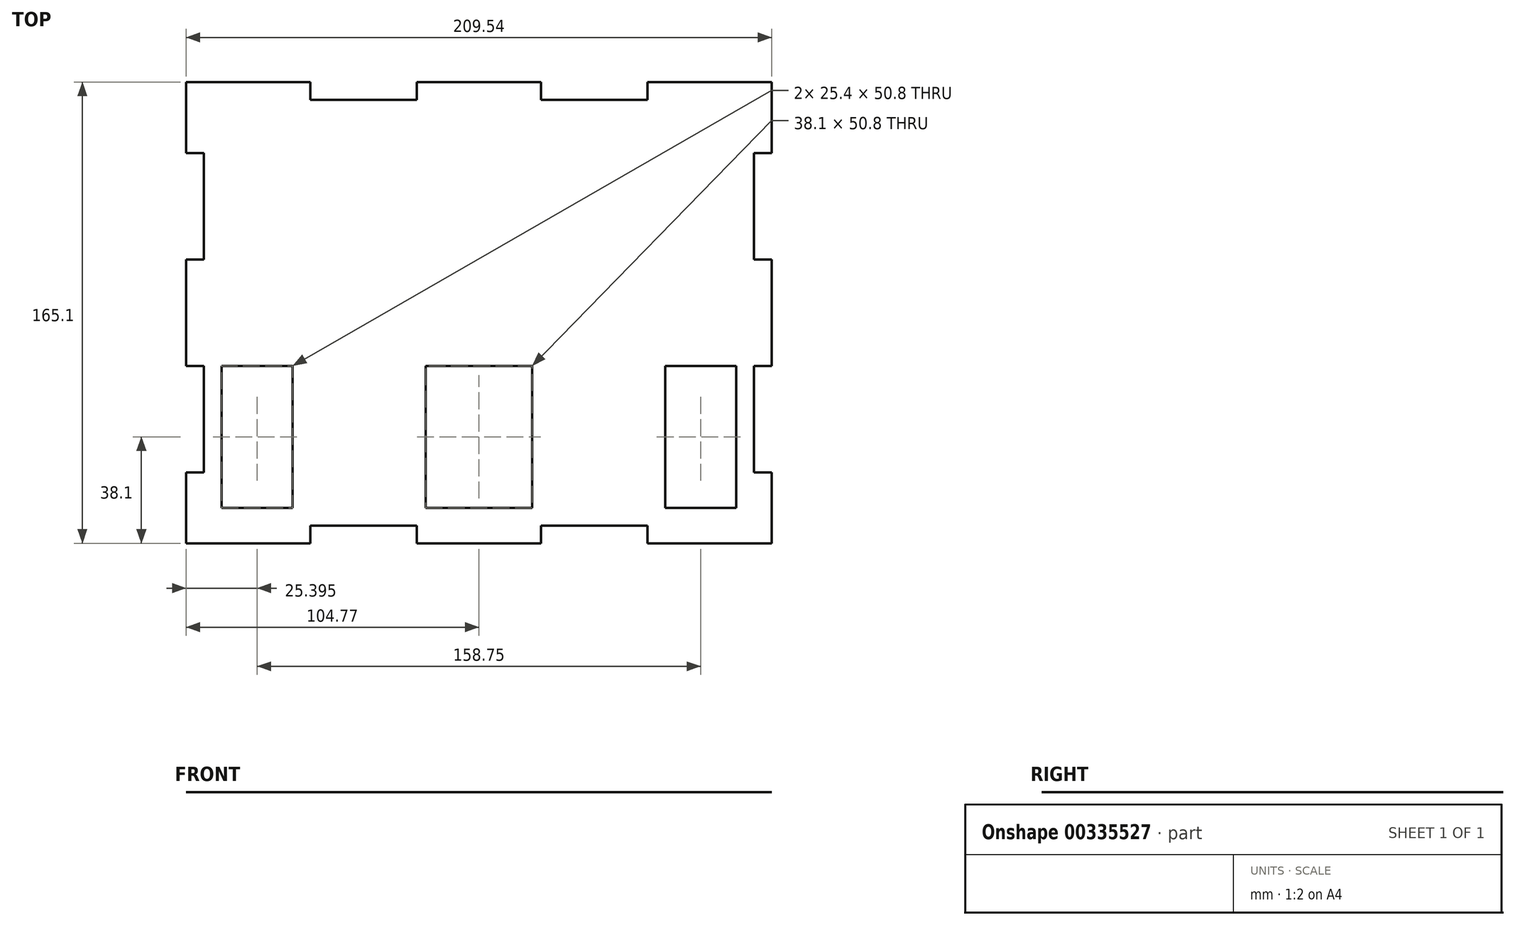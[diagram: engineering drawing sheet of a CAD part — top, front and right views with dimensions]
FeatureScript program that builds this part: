
annotation { "Feature Type Name" : "Feature", "Feature Type Description" : "" }
export const myFeature = defineFeature(function(context is Context, id is Id, definition is map)
    precondition{}
    {
        {
            var Q0;
            Q0=qCreatedBy(makeId("Top.planeOp"),FACE);
            var sketch = newSketch(context, id + "F0", { "sketchPlane" : qUnion([Q0])});
            skLineSegment(sketch, "E0.bottom", {"start": v(104.78, -82.55) * mm, "end": v(-104.77, -82.55) * mm});
            skLineSegment(sketch, "E0.top", {"start": v(104.77, 82.55) * mm, "end": v(-104.78, 82.55) * mm});
            skLineSegment(sketch, "E0.left", {"start": v(104.78, -82.55) * mm, "end": v(104.77, 82.55) * mm});
            skLineSegment(sketch, "E0.right", {"start": v(-104.77, -82.55) * mm, "end": v(-104.78, 82.55) * mm});
            skPoint(sketch, "E0.middle", {"position": v(0, 0) * mm});
            skSolve(sketch);
        }
        {
            var Q0;
            Q0=makeQuery(id+"F0.imprint","IMPRINT",FACE,{"disambiguationData":[TD([[makeQuery(id+"F0.imprint","IMPRINT",EDGE,{"derivedFrom":sQuery(id+"F0.wireOp",EDGE,"E0.bottom")}),-1.0]])]});
            extrude(context, id + "F1", {"entities" : qUnion([Q0]), "depth" : 1 / 203.2 * mm});
        }
        {
            var Q0;
            Q0=makeQuery(id+"F1.opExtrude","CAP_FACE",FACE,{"disambiguationData":[OSD([sQuery(id+"F0.wireOp",EDGE,"E0.bottom"),sQuery(id+"F0.wireOp",EDGE,"E0.top"),sQuery(id+"F0.wireOp",EDGE,"E0.left"),sQuery(id+"F0.wireOp",EDGE,"E0.right")])],"isStart":false});
            var sketch = newSketch(context, id + "F2", { "sketchPlane" : qUnion([Q0])});
            skLineSegment(sketch, "E1.bottom", {"start": v(-104.78, 57.15) * mm, "end": v(-98.43, 57.15) * mm});
            skLineSegment(sketch, "E1.top", {"start": v(-104.78, 19.05) * mm, "end": v(-98.43, 19.05) * mm});
            skLineSegment(sketch, "E1.left", {"start": v(-104.78, 57.15) * mm, "end": v(-104.78, 19.05) * mm});
            skLineSegment(sketch, "E1.right", {"start": v(-98.43, 57.15) * mm, "end": v(-98.43, 19.05) * mm});
            skLineSegment(sketch, "E2.bottom", {"start": v(-104.78, -57.15) * mm, "end": v(-98.43, -57.15) * mm});
            skLineSegment(sketch, "E2.top", {"start": v(-104.78, -19.05) * mm, "end": v(-98.43, -19.05) * mm});
            skLineSegment(sketch, "E2.left", {"start": v(-104.78, -57.15) * mm, "end": v(-104.78, -19.05) * mm});
            skLineSegment(sketch, "E2.right", {"start": v(-98.43, -57.15) * mm, "end": v(-98.43, -19.05) * mm});
            skLineSegment(sketch, "E3.MirrorCS", {"start": v(98.43, 57.15) * mm, "end": v(98.43, 19.05) * mm});
            skLineSegment(sketch, "E4.MirrorCS", {"start": v(104.78, 19.05) * mm, "end": v(98.43, 19.05) * mm});
            skLineSegment(sketch, "E5.MirrorCS", {"start": v(104.78, 57.15) * mm, "end": v(104.78, 19.05) * mm});
            skLineSegment(sketch, "E6.MirrorCS", {"start": v(104.78, 57.15) * mm, "end": v(98.43, 57.15) * mm});
            skLineSegment(sketch, "E7.MirrorCS", {"start": v(104.78, -19.05) * mm, "end": v(98.43, -19.05) * mm});
            skLineSegment(sketch, "E8.MirrorCS", {"start": v(104.78, -57.15) * mm, "end": v(104.78, -19.05) * mm});
            skLineSegment(sketch, "E9.MirrorCS", {"start": v(104.78, -57.15) * mm, "end": v(98.43, -57.15) * mm});
            skLineSegment(sketch, "E10.MirrorCS", {"start": v(98.43, -57.15) * mm, "end": v(98.43, -19.05) * mm});
            skLineSegment(sketch, "E11.bottom", {"start": v(-60.33, -82.55) * mm, "end": v(-22.23, -82.55) * mm});
            skLineSegment(sketch, "E11.top", {"start": v(-60.32, -76.2) * mm, "end": v(-22.22, -76.2) * mm});
            skLineSegment(sketch, "E11.left", {"start": v(-60.32, -82.55) * mm, "end": v(-60.32, -76.2) * mm});
            skLineSegment(sketch, "E11.right", {"start": v(-22.23, -82.55) * mm, "end": v(-22.23, -76.2) * mm});
            skLineSegment(sketch, "E12.bottom", {"start": v(22.23, -82.55) * mm, "end": v(60.33, -82.55) * mm});
            skLineSegment(sketch, "E12.top", {"start": v(22.23, -76.2) * mm, "end": v(60.33, -76.2) * mm});
            skLineSegment(sketch, "E12.left", {"start": v(22.23, -82.55) * mm, "end": v(22.23, -76.2) * mm});
            skLineSegment(sketch, "E12.right", {"start": v(60.33, -82.55) * mm, "end": v(60.33, -76.2) * mm});
            skLineSegment(sketch, "E13.MirrorCS", {"start": v(22.23, 82.55) * mm, "end": v(22.23, 76.2) * mm});
            skLineSegment(sketch, "E14.MirrorCS", {"start": v(22.23, 76.2) * mm, "end": v(60.33, 76.2) * mm});
            skLineSegment(sketch, "E15.MirrorCS", {"start": v(22.23, 82.55) * mm, "end": v(60.33, 82.55) * mm});
            skLineSegment(sketch, "E16.MirrorCS", {"start": v(60.33, 82.55) * mm, "end": v(60.33, 76.2) * mm});
            skLineSegment(sketch, "E17.MirrorCS", {"start": v(-22.23, 82.55) * mm, "end": v(-22.23, 76.2) * mm});
            skLineSegment(sketch, "E18.MirrorCS", {"start": v(-60.33, 82.55) * mm, "end": v(-22.23, 82.55) * mm});
            skLineSegment(sketch, "E19.MirrorCS", {"start": v(-60.33, 82.55) * mm, "end": v(-60.33, 76.2) * mm});
            skLineSegment(sketch, "E20.MirrorCS", {"start": v(-60.32, 76.2) * mm, "end": v(-22.22, 76.2) * mm});
            skSolve(sketch);
        }
        {
            var Q0;
            Q0 = qSketchRegion(id + "F2", true);
            extrude(context, id + "F3", {"entities" : qUnion([Q0]), "operationType" : NewBodyOperationType.REMOVE, "oppositeDirection" : true, "depth" : 25.4 * mm});
        }
        {
            var Q0;
            Q0=makeQuery(id+"F1.opExtrude","CAP_FACE",FACE,{"disambiguationData":[OSD([sQuery(id+"F0.wireOp",EDGE,"E0.bottom"),sQuery(id+"F0.wireOp",EDGE,"E0.top"),sQuery(id+"F0.wireOp",EDGE,"E0.left"),sQuery(id+"F0.wireOp",EDGE,"E0.right")])],"isStart":false});
            var sketch = newSketch(context, id + "F4", { "sketchPlane" : qUnion([Q0])});
            skLineSegment(sketch, "E21.bottom", {"start": v(-92.08, -19.05) * mm, "end": v(-66.68, -19.05) * mm});
            skLineSegment(sketch, "E21.top", {"start": v(-92.08, -69.85) * mm, "end": v(-66.67, -69.85) * mm});
            skLineSegment(sketch, "E21.left", {"start": v(-92.08, -19.05) * mm, "end": v(-92.08, -69.85) * mm});
            skLineSegment(sketch, "E21.right", {"start": v(-66.68, -19.05) * mm, "end": v(-66.67, -69.85) * mm});
            skLineSegment(sketch, "E22.MirrorCS", {"start": v(66.68, -19.05) * mm, "end": v(66.67, -69.85) * mm});
            skLineSegment(sketch, "E23.MirrorCS", {"start": v(92.08, -19.05) * mm, "end": v(92.08, -69.85) * mm});
            skLineSegment(sketch, "E24.MirrorCS", {"start": v(92.08, -69.85) * mm, "end": v(66.67, -69.85) * mm});
            skLineSegment(sketch, "E25.MirrorCS", {"start": v(92.08, -19.05) * mm, "end": v(66.68, -19.05) * mm});
            skLineSegment(sketch, "E26.bottom", {"start": v(19.05, -69.85) * mm, "end": v(-19.05, -69.85) * mm});
            skLineSegment(sketch, "E26.top", {"start": v(19.05, -19.05) * mm, "end": v(-19.05, -19.05) * mm});
            skLineSegment(sketch, "E26.left", {"start": v(19.05, -69.85) * mm, "end": v(19.05, -19.05) * mm});
            skLineSegment(sketch, "E26.right", {"start": v(-19.05, -69.85) * mm, "end": v(-19.05, -19.05) * mm});
            skPoint(sketch, "E26.middle", {"position": v(0, -44.45) * mm});
            skSolve(sketch);
        }
        {
            var Q0;
            Q0 = qSketchRegion(id + "F4", true);
            extrude(context, id + "F5", {"entities" : qUnion([Q0]), "operationType" : NewBodyOperationType.REMOVE, "oppositeDirection" : true, "depth" : 25.4 * mm});
        }
    });
